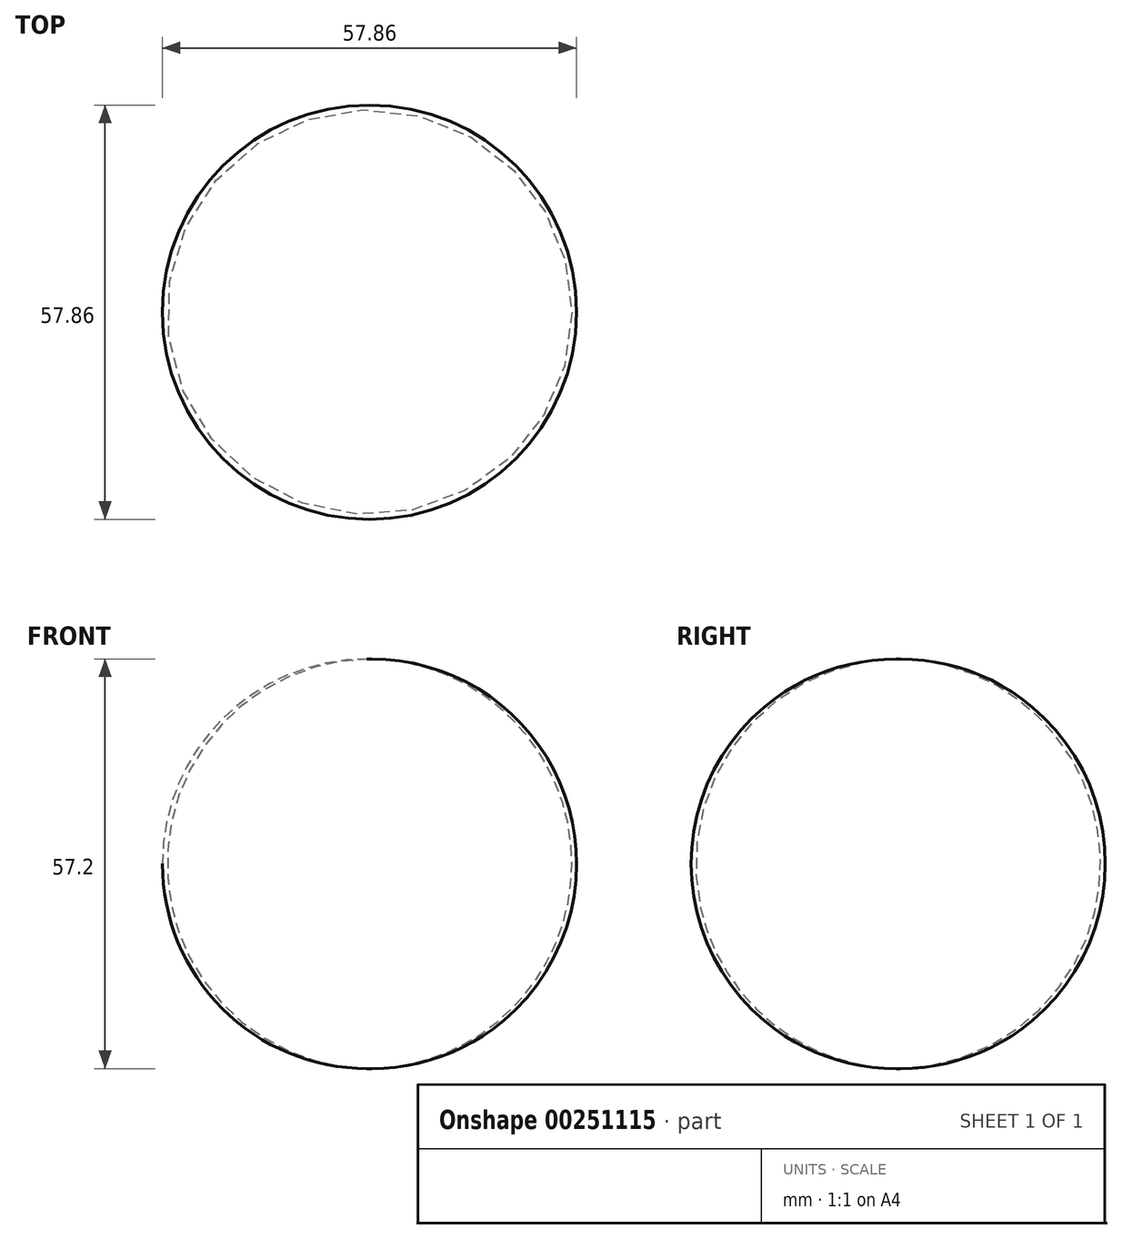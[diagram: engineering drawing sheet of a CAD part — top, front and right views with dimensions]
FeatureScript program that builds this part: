
annotation { "Feature Type Name" : "Feature", "Feature Type Description" : "" }
export const myFeature = defineFeature(function(context is Context, id is Id, definition is map)
    precondition{}
    {
        {
            var Q0;
            Q0=qCreatedBy(makeId("Front.planeOp"),FACE);
            var sketch = newSketch(context, id + "F0", { "sketchPlane" : qUnion([Q0])});
            skLineSegment(sketch, "E0", {"start": v(0, 0) * mm, "end": v(0, 57.2) * mm});
            skArc(sketch, "E1", {"start": v(0, 0) * mm, "mid": v(28.93, 28.6) * mm, "end": v(0, 57.2) * mm});
            skSolve(sketch);
        }
        {
            var Q0;
            Q0=makeQuery(id+"F0.imprint","IMPRINT",FACE,{"disambiguationData":[TD([[makeQuery(id+"F0.imprint","IMPRINT",EDGE,{"derivedFrom":sQuery(id+"F0.wireOp",EDGE,"E0")}),-1.0]])]});
            var Q1;
            Q1=sQuery(id+"F0.wireOp",EDGE,"E0");
            revolve(context, id + "F1", {"entities" : qUnion([Q0]), "axis" : qUnion([Q1]), "revolveType" : RevolveType.FULL});
        }
    });
